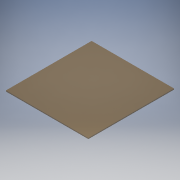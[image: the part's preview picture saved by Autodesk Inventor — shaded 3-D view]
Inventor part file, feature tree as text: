
AUTODESK INVENTOR PART (.ipt)
format: ipt  version: 2016 (Build 200138000, 138)  size: 93,184 bytes
history: native  units: in
note: dims shown in document units (in); Inventor stores cm internally (conversion verified against a paired STEP export)
features: extrude x1, sketch x1
ambient origin geometry x8: Origin, YZ Plane, XZ Plane, XY Plane, X Axis, Y Axis, Z Axis, Center Point
bodies: Solid1 (feature_tree)
feature tree (2):
  extrude  "Extrusion1"  TaperAngle=90.0deg  [1 undecoded]
  sketch  "Sketch1"  dims[d0=88.375in d1=90.0deg d2=85.0in d3=1.0in d4=0.0in]
note: 1 required parameter value undecoded (feature->parameter linkage not recoverable at this tier; creation-order binding heuristic only, values carry confidence <= 0.55)
